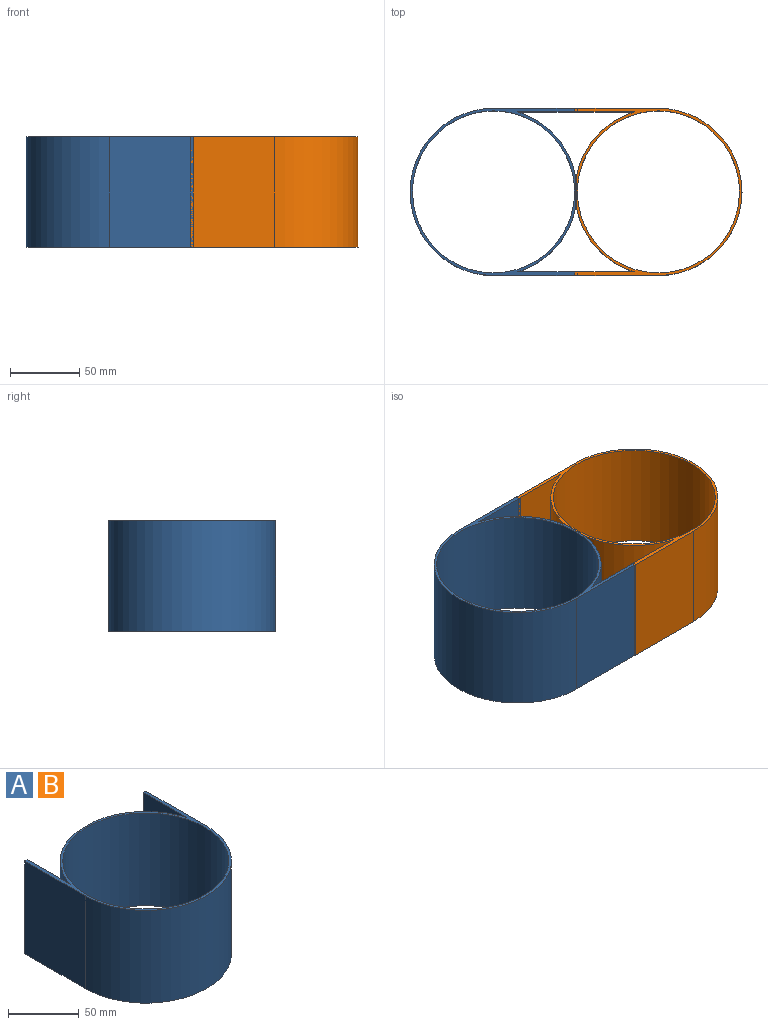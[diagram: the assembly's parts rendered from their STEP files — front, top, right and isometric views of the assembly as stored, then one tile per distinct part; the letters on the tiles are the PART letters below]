
ASSEMBLY  parts=2 mates=1
PART A: 13 faces, bbox 120.9x120.9x80 mm
  f0: plane 80x19.93mm, normal (0,1,0), area 1594.5mm2, adj f1,f10,f11,f12
  f1: cylinder r=60.44mm len=80mm, axis (0,0,1), area 5377.3mm2, adj f0,f2,f11,f12
  f2: plane 80x42.98mm, normal (1,0,0), area 3438.4mm2, adj f1,f3,f11,f12
  f3: plane 80x2.58mm, normal (0,1,0), area 206.2mm2, adj f2,f4,f11,f12
  f4: plane 80x60.44mm, normal (-1,0,0), area 4835.4mm2, adj f3,f5,f11,f12
  f5: cylinder r=60.44mm len=120.88mm, axis (0,0,1), area 15190.7mm2, adj f4,f6,f11,f12
  f6: plane 80x60.44mm, normal (1,0,0), area 4835.4mm2, adj f5,f7,f11,f12
  f7: plane 80x2.58mm, normal (0,1,0), area 206.2mm2, adj f6,f8,f11,f12
  f8: plane 80x42.98mm, normal (-1,0,0), area 3438.4mm2, adj f7,f10,f11,f12
  f9: cylinder r=58.59mm len=117.19mm, axis (0,0,1), area 29452.2mm2, adj f11,f12
  f10: cylinder r=60.44mm len=80mm, axis (0,0,1), area 5377.3mm2, adj f0,f8,f11,f12
  f11: plane 120.88x120.88mm, normal (0,0,1), area 931.6mm2, adj f0,f1,f2,f3,f4,f5,f6,f7
  f12: plane 120.88x120.88mm, normal (0,0,-1), area 931.6mm2, adj f0,f1,f2,f3,f4,f5,f6,f7
PART B: same geometry as A
PLACE A rot(axis=(0.71,0.71,0),180deg) t=(-60.26,0.5,-18.25)mm
PLACE B rot(axis=(0,0,1),90deg) t=(58.97,0.5,-98.25)mm
MATE fastened B.f0 <-> A.f0  axis (-1,0,0) through (-0.65,0.5,-58.25)mm
